# Revit family: Sanitary_Basins_Johnson-Suisse_Emilia_450_wall_basin
name_source: partatom
category: Plumbing Fixtures
revit_build: Autodesk Revit 2015 (Build: 20140606_1530(x64)
units: mm (PartAtom-declared; Revit-internal decimal feet)

## types (1)
- Emilia 450 wall basin
    BIMobject category = Basins
    Brand url = http://www.johnsonsuisse.com.au
    Design country = Spain
    EAN code = https://9325304002712
    Edition number = 1
    IFC Classification = Sanitary Terminal
    Manufacturer country = Bulgaria
    Manufacturer name = Johnson Suisse
    Material main = Vitreous china
    NBS Reference Code = 35-79-94
    NBS Reference Description = Wall-Hung Wash Basins
    Nominal height = 160 mm  [stored 0.524934 ft]
    Nominal width = 455 mm  [stored 1.49278 ft]
    Product Guid = 8874a2e2-8a9b-4c05-be3b-8d53640a97d0
    Product SKU = J3140-1
    Product data url = https://bimobject.com
    Product family = Emilia
    Product group = Basins
    Product url = https://johnsonsuisse.com.au
    QR code = http://bimobject.com
    Technical description = https://johnsonsuisse.com.au
    Type = emilia_450_wall_basin : Default
    UNSPSC Code = 301815
    Uniclass 1.4 Code = L7212
    Uniclass 1.4 Description = Washbasins
    Uniclass 2.0 Code = PR-35-79-94
    Uniclass 2.0 Description = Wall-Hung Wash Basins
    Uniclass 2015 Code = Pr_40_20_96_96
    Uniclass 2015 Name = Wall-hung wash basins
    Weight Net (Kg) = 17

note: [stored X ft] marks values corroborated as IEEE doubles in the binary element streams (Revit-internal decimal feet)

## geometry (parser evidence)
native form markers: Sweep x4
no freeform markers — native parametric forms only
